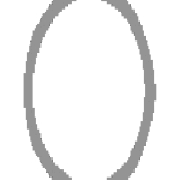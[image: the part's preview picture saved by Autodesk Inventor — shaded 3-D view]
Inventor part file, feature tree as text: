
AUTODESK INVENTOR PART (.ipt)
format: ipt  version: 2021 (Build 250183000, 183)  size: 109,568 bytes
history: native  units: in
note: dims shown in document units (in); Inventor stores cm internally (conversion verified against a paired STEP export)
features: other x4, sketch x3, plane x1
ambient origin geometry x8: Origin, YZ Plane, XZ Plane, XY Plane, X Axis, Y Axis, Z Axis, Center Point
bodies: Solid1 (feature_tree), Body (feature_tree)
feature tree (8):
  other  "Driven Length"
  other  "Frame Generator"
  other  "Start Plane"
  other  "End Plane"
  sketch  "Sketch"  dims[d2=13.0in d4=-0.0in d5=13.0in d6=0.12in d7=0.0in d8=90.0deg d9=13.0in]
  sketch  "Sketch2"  dims[d0=1.0in]
  plane  "Work Plane3"
  sketch  "Sketch3"  dims[d1=0.065in]
